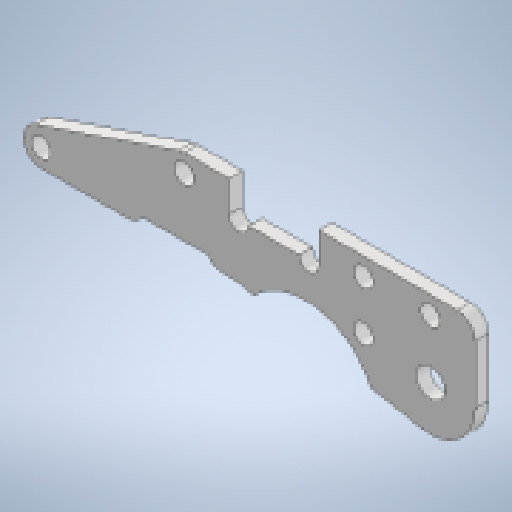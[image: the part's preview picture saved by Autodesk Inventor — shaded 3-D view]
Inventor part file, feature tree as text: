
AUTODESK INVENTOR PART (.ipt)
format: ipt  version: 2025.1 (Build 291241000, 241)  size: 293,888 bytes
history: native  units: mm
features: other x4, reference x4, extrude x2, sketch x2, fillet x1
ambient origin geometry x8: Origin, YZ Plane, XZ Plane, XY Plane, X Axis, Y Axis, Z Axis, Center Point
bodies: Body1 (feature_tree)
feature tree (13):
  other  "ソリッド1"
  extrude  "押し出し1"  Depth=2.2mm
  extrude  "押し出し3"  Depth=2.2mm
  fillet  "フィレット2"  Radius=36.0mm
  sketch  "スケッチ1"
  sketch  "スケッチ3"
  reference  "参照3"
  reference  "参照4"
  reference  "参照5"
  reference  "参照6"
  other  "Assembly1"
  other  "02157_SmallDiameterHornB:3"
  other  "KRS2500_scale:3"
